# Revit family: Keilhauer_Pact_Bench_Booth Divider_77611
name_source: partatom
category: Furniture
revit_build: Autodesk Revit 2017 (Build: 20160225_1515(x64)
units: mm (PartAtom-declared; Revit-internal decimal feet)

## family parameters
Always vertical = Yes
Cut with Voids When Loaded = No
OmniClass Number = 23.40.70.14.64.11
OmniClass Title = Office Furniture
Room Calculation Point = No
Shared = No
Work Plane-Based = No

## types (4) — shared parameters
Assembly Code = E2020200
Catalog = Pact
Manufacturer = Keilhauer, Corp.
Product Documentation Link = http://www.keilhauer.com
URL = http://www.keilhauer.com

## per-type parameters (varying)
| type | Config | Description | Length | Model | Privacy | Size |
| 57" Adjoining Privacy booth | 2 | Pact 57" Adjoining Privacy booth | 28.498 " | 77611 | Yes | 2 |
| 57" Privacy booth | 1 | Pact 57" Privacy booth | 28.498 " | 77610 | No | 2 |
| 32" Adjoining Privacy booth | 2 | Pact 32" Adjoining Privacy booth | 16 " | 77601 | Yes | 1 |
| 32" Privacy booth | 1 | Pact 32" Privacy booth | 16 " | 77600 | No | 1 |

## geometry (parser evidence)
native form markers: Sweep x3
no freeform markers — native parametric forms only
